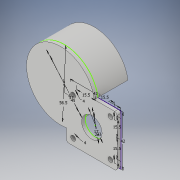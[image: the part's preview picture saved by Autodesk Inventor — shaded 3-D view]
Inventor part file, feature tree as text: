
AUTODESK INVENTOR PART (.ipt)
format: ipt  version: 2018 (Build 220112000, 112)  size: 161,280 bytes
history: native  units: in
note: dims shown in document units (in); Inventor stores cm internally (conversion verified against a paired STEP export)
features: extrude x3, sketch x1, fillet x1
ambient origin geometry x8: Origin, YZ Plane, XZ Plane, XY Plane, X Axis, Y Axis, Z Axis, Center Point
bodies: Solid1 (feature_tree)
feature tree (5):
  sketch  "Sketch1"  dims[d0=1.6535in d1=1.6535in d2=0.9055in d3=0.6102in d4=0.6102in d5=0.6102in d6=0.6102in d7=0.1575in d8=0.1575in d9=0.1575in d10=0.1575in d11=0.9449in d15=1.4567in d16=1.7717in d17=0.6693in d18=2.2244in d19=1.8307in d20=0.2362in d21=0.1181in d22=0.0in d23=0.9843in d24=0.0in d25=0.8661in d26=0.0in d27=0.0787in]
  extrude  "Extrusion1"  Depth=1.6535in
  extrude  "Extrusion2"  Depth=0.0787in
  extrude  "Extrusion3"  Depth=0.0787in
  fillet  "Fillet1"  Radius=0.6102in
